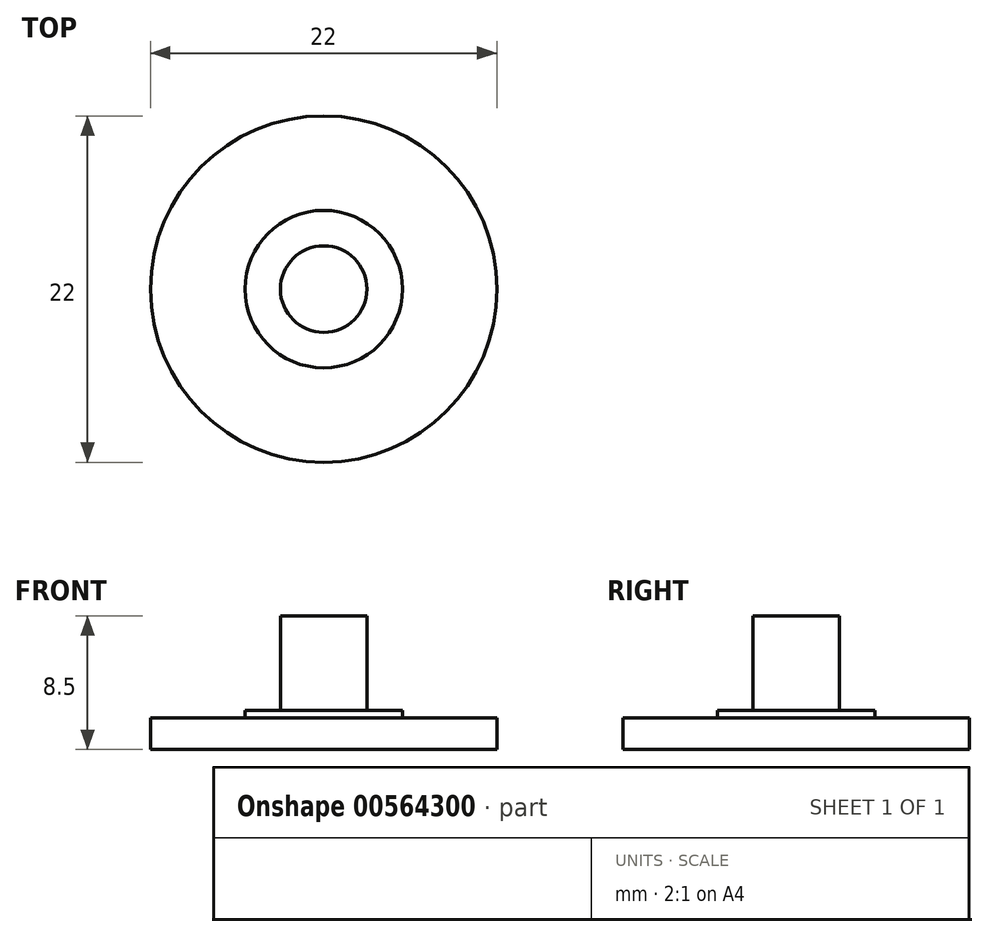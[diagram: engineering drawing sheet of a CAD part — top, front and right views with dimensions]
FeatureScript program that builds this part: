
annotation { "Feature Type Name" : "Feature", "Feature Type Description" : "" }
export const myFeature = defineFeature(function(context is Context, id is Id, definition is map)
    precondition{}
    {
        {
            var Q0;
            Q0=qCreatedBy(makeId("Top.planeOp"),FACE);
            var sketch = newSketch(context, id + "F0", { "sketchPlane" : qUnion([Q0])});
            skCircle(sketch, "E0", {"center": v(0, 0) * mm, "radius": 11 * mm});
            skSolve(sketch);
        }
        {
            var Q0;
            Q0=makeQuery(id+"F0.imprint","IMPRINT",FACE,{"disambiguationData":[TD([[makeQuery(id+"F0.imprint","IMPRINT",EDGE,{"derivedFrom":sQuery(id+"F0.wireOp",EDGE,"E0")}),1.0]])]});
            extrude(context, id + "F1", {"entities" : qUnion([Q0]), "depth" : 2 * mm, "offsetDistance" : 25 * mm});
        }
        {
            var Q0;
            Q0=makeQuery(id+"F1.opExtrude","CAP_FACE",FACE,{"disambiguationData":[OSD([sQuery(id+"F0.wireOp",EDGE,"E0")])],"isStart":false});
            var sketch = newSketch(context, id + "F2", { "sketchPlane" : qUnion([Q0])});
            skCircle(sketch, "E1", {"center": v(0, 0) * mm, "radius": 5 * mm});
            skSolve(sketch);
        }
        {
            var Q0;
            Q0=makeQuery(id+"F2.imprint","IMPRINT",FACE,{"disambiguationData":[TD([[makeQuery(id+"F2.imprint","IMPRINT",EDGE,{"derivedFrom":sQuery(id+"F2.wireOp",EDGE,"E1")}),1.0]])]});
            extrude(context, id + "F3", {"entities" : qUnion([Q0]), "operationType" : NewBodyOperationType.ADD, "depth" : .5 * mm, "offsetDistance" : 25 * mm});
        }
        {
            var Q0;
            Q0=makeQuery(id+"F3.opExtrude","CAP_FACE",FACE,{"disambiguationData":[OSD([sQuery(id+"F2.wireOp",EDGE,"E1")])],"isStart":false});
            var sketch = newSketch(context, id + "F4", { "sketchPlane" : qUnion([Q0])});
            skCircle(sketch, "E2", {"center": v(0, 0) * mm, "radius": 2.75 * mm});
            skSolve(sketch);
        }
        {
            var Q0;
            Q0=makeQuery(id+"F4.imprint","IMPRINT",FACE,{"disambiguationData":[TD([[makeQuery(id+"F4.imprint","IMPRINT",EDGE,{"derivedFrom":sQuery(id+"F4.wireOp",EDGE,"E2")}),1.0]])]});
            extrude(context, id + "F5", {"entities" : qUnion([Q0]), "operationType" : NewBodyOperationType.ADD, "depth" : 6 * mm, "offsetDistance" : 25 * mm});
        }
    });
